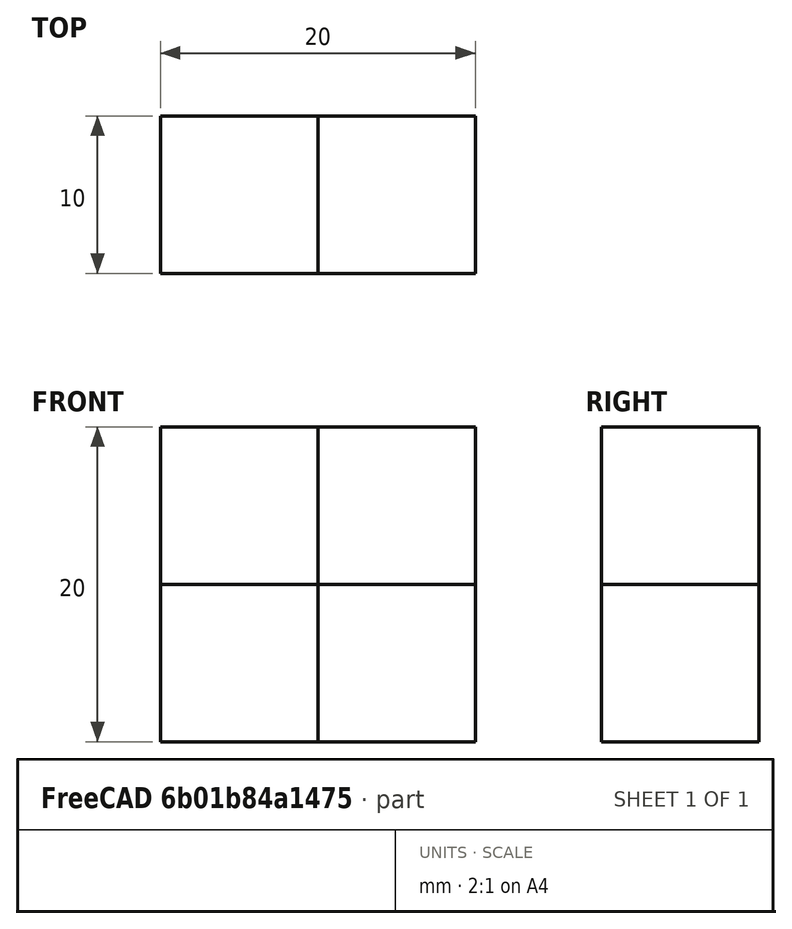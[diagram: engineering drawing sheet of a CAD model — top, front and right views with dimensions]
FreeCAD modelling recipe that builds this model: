
FCSTD DOCUMENT  (FreeCAD 0.21R33694 (Git))
Label: prestress_test
License: All rights reserved
LicenseURL: http://en.wikipedia.org/wiki/All_rights_reserved
objects: Part::Box×4, Fem::ConstraintForce×3, Fem::ConstraintDisplacement×2, Fem::FemMeshObjectPython×2, App::MaterialObjectPython×2, Fem::FemSolverObjectPython×1, Part::FeaturePython×1, Fem::FemAnalysis×1
note: 5 computed .brp shape members not serialized (recipe doc carries the construction recipe); baked Part::Feature solids carry a one-line shape summary decoded from their .brp

FEATURE [Part::Box] Box  label="Cube"
  AttacherType = Attacher::AttachEngine3D
  Height = 10
  Length = 10
  Width = 10
FEATURE [Part::Box] Box001  label="Cube001"
  AttacherType = Attacher::AttachEngine3D
  Height = 10
  Length = 10
  Placement = pos=(10,0,0) rot=(0,0,1;0rad)
  Width = 10
FEATURE [Fem::ConstraintDisplacement] ConstraintDisplacement
  NormalDirection = (0,0,1)
  Normals = (2) [(0,0,1),(0,0,1)]
  Points = (2) [(0,0,0),(0,10,0)]
  References = -> [Box]
  hasXFormula = false
  hasYFormula = false
  hasZFormula = false
  rotxFix = false
  rotxFree = true
  rotyFix = false
  rotyFree = true
  rotzFix = false
  rotzFree = true
  useFlowSurfaceForce = false
  xDisplacement = 0
  xFix = false
  xFree = false
  xRotation = 0
  yDisplacement = 0
  yFix = false
  yFree = false
  yRotation = 0
  zDisplacement = 0
  zFix = false
  zFree = false
  zRotation = 0
FEATURE [Fem::ConstraintDisplacement] ConstraintDisplacement001
  NormalDirection = (0,0,1)
  Normals = (2) [(0,0,1),(0,0,1)]
  Points = (2) [(20,0,0),(20,10,0)]
  References = -> [Box001]
  hasXFormula = false
  hasYFormula = false
  hasZFormula = false
  rotxFix = false
  rotxFree = true
  rotyFix = false
  rotyFree = true
  rotzFix = false
  rotzFree = true
  useFlowSurfaceForce = false
  xDisplacement = 0
  xFix = false
  xFree = true
  xRotation = 0
  yDisplacement = 0
  yFix = false
  yFree = false
  yRotation = 0
  zDisplacement = 0
  zFix = false
  zFree = false
  zRotation = 0
FEATURE [Fem::FemMeshObjectPython] FEMMeshGmsh  # FEM object (typed FeaturePython)
  Algorithm2D = 0
  Algorithm3D = 0
  CharacteristicLengthMax = 10
  CharacteristicLengthMin = 0
  CoherenceMesh = true
  ElementDimension = 0
  ElementOrder = 1
  GeometryTolerance = 1e-06
  GroupsOfNodes = false
  HighOrderOptimize = 0
  MeshSizeFromCurvature = 12
  OptimizeNetgen = false
  OptimizeStd = true
  RecombinationAlgorithm = 0
  Recombine3DAll = false
  RecombineAll = false
  SecondOrderLinear = false
FEATURE [Fem::ConstraintForce] ConstraintForce  label="ConstraintForce(p)"
  DirectionVector = (1,0,0)
  Force = 10000
  NormalDirection = (-1,0,0)
  Points = (9) [(0,10,0),(0,10,5),(0,10,10),(0,5,0),(0,5,5),(0,5,10),(0,0,0),(0,0,5),(0,0,10)]
  References = -> [Box]
  Reversed = true
FEATURE [Fem::ConstraintForce] ConstraintForce001  label="ConstraintForce001(p)"
  DirectionVector = (-1,0,0)
  Force = 10000
  NormalDirection = (1,0,0)
  Points = (9) [(20,10,0),(20,10,5),(20,10,10),(20,5,0),(20,5,5),(20,5,10),(20,0,0),(20,0,5),(20,0,10)]
  References = -> [Box001]
  Reversed = true
FEATURE [Fem::FemSolverObjectPython] SolverCcxTools  # FEM object (typed FeaturePython)
  AnalysisType = 0
  BeamShellResultOutput3D = false
  BucklingFactors = 1
  EigenmodeHighLimit = 1000000
  EigenmodeLowLimit = 0
  EigenmodesCount = 10
  GeometricalNonlinearity = 0
  IterationsControlParameterCutb = 0.25,0.5,0.75,0.85,,,1.5,
  IterationsControlParameterIter = 4,8,9,200,10,400,,200,,
  IterationsControlParameterTimeUse = false
  IterationsThermoMechMaximum = 2000
  IterationsUserDefinedIncrementations = false
  IterationsUserDefinedTimeStepLength = false
  MaterialNonlinearity = 0
  MatrixSolverType = 0
  SplitInputWriter = false
  ThermoMechSteadyState = true
  TimeEnd = 1
  TimeInitialStep = 0.01
FEATURE [Part::Box] Box002  label="Cube002"
  AttacherType = Attacher::AttachEngine3D
  Height = 10
  Length = 10
  Placement = pos=(0,0,10) rot=(0,0,1;0rad)
  Width = 10
FEATURE [App::MaterialObjectPython] MaterialSolid  # material (typed FeaturePython)
  Category = 0
  Material = AuthorAndLicense=(c) 2014 M. Münch - GNU Lesser General Public License (LGPL); CardName=Steel-St-E-315; Density=7800 kg/m^3; Father=Metal; KindOfMaterial=Fine grain steel; KindOfMaterialDE=Feinkornstahl; MaterialNumber=1.0505; Name=St E 315; NameDE=St E 315; Norm=DIN 17102; PoissonRatio=0.3; ShearModulus=81000 MPa; ThermalExpansionCoefficient=0.000011 m/m/K; UltimateStrain=0; UltimateTensileStrength=440 MPa; YieldStrength=320 MPa; YoungsModulus=210000 MPa
  References = -> [Box,Box002]
FEATURE [Part::Box] Box003  label="Cube003"
  AttacherType = Attacher::AttachEngine3D
  Height = 10
  Length = 10
  Placement = pos=(10,0,10) rot=(0,0,1;0rad)
  Width = 10
FEATURE [App::MaterialObjectPython] MaterialSolid001  # material (typed FeaturePython)
  Category = 0
  Material = AuthorAndLicense=(c) 2014 M. Münch - GNU Lesser General Public License (LGPL); CardName=Steel-St-E-315; Density=7800 kg/m^3; Father=Metal; KindOfMaterial=Fine grain steel; KindOfMaterialDE=Feinkornstahl; MaterialNumber=1.0505; Name=St E 315; NameDE=St E 315; Norm=DIN 17102; PoissonRatio=0.3; ShearModulus=81000 MPa; ThermalExpansionCoefficient=0.000011 m/m/K; UltimateStrain=0; UltimateTensileStrength=440 MPa; YieldStrength=320 MPa; YoungsModulus=210000 MPa
  References = -> [Box001,Box003]
FEATURE [Part::FeaturePython] BooleanFragments  # WARN: FeaturePython — macro-defined, semantics opaque (R4)
  Mode = 0
  Objects = -> [Box,Box001,Box002,Box003]
  Tolerance = 0
FEATURE [Fem::FemMeshObjectPython] FEMMeshGmsh001  # FEM object (typed FeaturePython)
  Algorithm2D = 0
  Algorithm3D = 0
  CharacteristicLengthMax = 10
  CharacteristicLengthMin = 0
  CoherenceMesh = true
  ElementDimension = 0
  ElementOrder = 1
  GeometryTolerance = 1e-06
  GroupsOfNodes = false
  HighOrderOptimize = 0
  MeshSizeFromCurvature = 12
  OptimizeNetgen = false
  OptimizeStd = true
  Part = -> BooleanFragments
  RecombinationAlgorithm = 0
  Recombine3DAll = false
  RecombineAll = false
  SecondOrderLinear = false
FEATURE [Fem::ConstraintForce] ConstraintForce002
  DirectionVector = (0,0,-1)
  Force = 10000
  NormalDirection = (0,0,1)
  Points = (18) [(0,0,20),(5,0,20),(10,0,20),(0,5,20),(5,5,20),(10,5,20),(0,10,20),(5,10,20),(10,10,20),(10,0,20),(15,0,20),(20,0,20),(10,5,20),(15,5,20),(20,5,20),(10,10,20),(15,10,20),(20,10,20)]
  References = -> [Box002,Box003]
  Reversed = true
FEATURE [Fem::FemAnalysis] Analysis
  Group = -> [ConstraintDisplacement,ConstraintDisplacement001,MaterialSolid,MaterialSolid001,FEMMeshGmsh,ConstraintForce,ConstraintForce001,SolverCcxTools,FEMMeshGmsh001,ConstraintForce002]
